# Revit family: Appliance_Cabinet-Danver-Side_Burner_Base
name_source: partatom
category: Casework
units: mm (PartAtom-declared; Revit-internal decimal feet)

## family parameters
Always vertical = Yes
Classification Number = 23.40.35.11.11
Cut with Voids When Loaded = No
Room Calculation Point = No
Shared = No
Work Plane-Based = No

## types (1)
- Not a Type - Load Type Catalog
    Cabinet Material = Metal - Danver - Stainless Steel
    Construction Type = 304 Grade Stainless Steel
    Default Elevation = 0' - 0"
    Depth = 2' - 0"
    Depth+Door = 2' - 0 7/8"
    Description = Please Load Accompanying Type Catalog (.txt)
    Door Count = 0
    Door Material = Metal - Danver - Stainless Steel
    Door Panel Material = Metal - Danver - Stainless Steel
    Drawer Count = 2
    Drawer Height = 0' - 10 1/4"
    Grill Box Depth = 0' - 9 1/4"
    Grill Offset = 0' - 10"
    Grill Width = 1' - 0"
    Handle Material = Metal - Danver - Chrome Plated Steel
    Height = 2' - 6"
    Manufacturer = Danver Outdoor Kitchens
    Manufacturer Note = Generic Burner shown, contact Danver for more information
    Model = Please Load Accompanying Type Catalog (.txt)
    Product Documentation Link = https://danver.com
    Product Name = Appliance Cabinet - Danver - Side Burner Base - 1 Door
    Product Page URL = https://danver.com
    Toe Height = 0' - 4 1/2"
    Toe Kick Material = Metal - Danver - Toe Kick
    URL = www.danver.com
    V_Door1 = No
    V_Door2 = No
    V_Drawer = Yes
    Version = 2019 - V1.0b
    Width = 1' - 3"

## geometry (parser evidence)
native form markers: Sweep x24
no freeform markers — native parametric forms only
